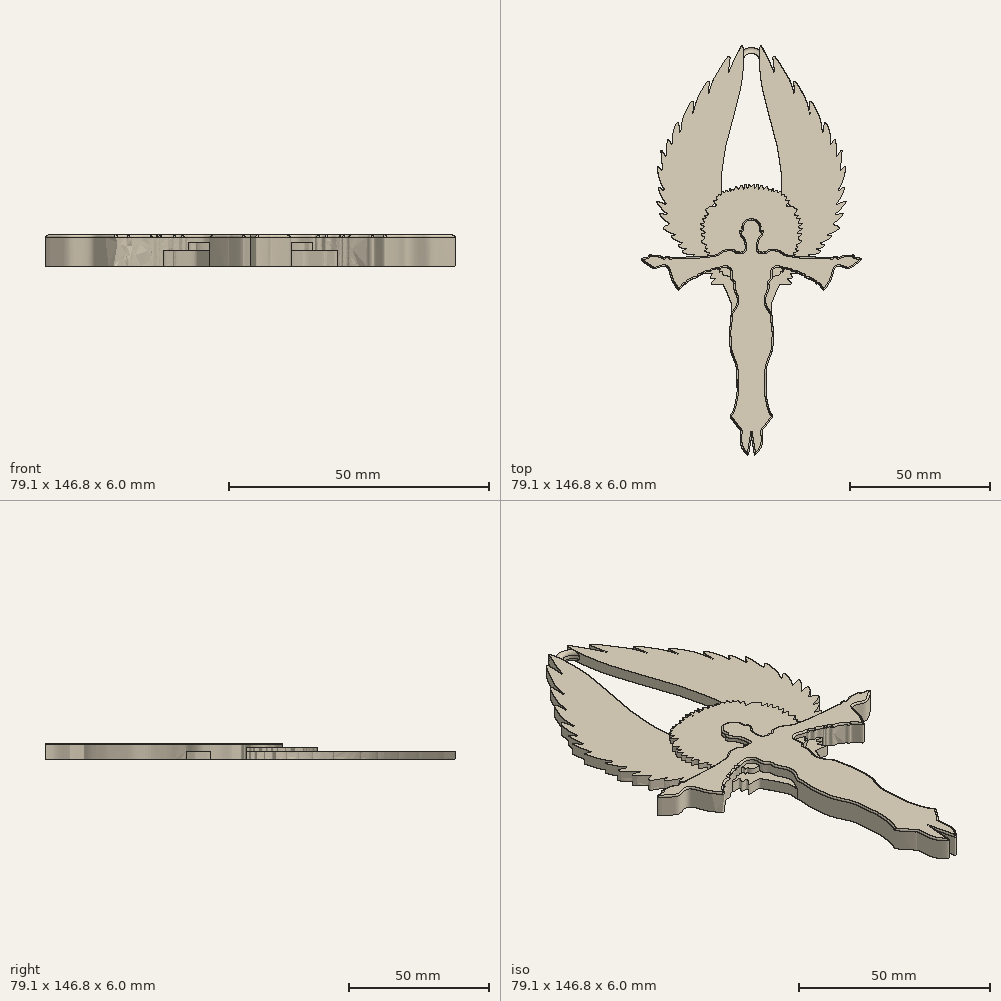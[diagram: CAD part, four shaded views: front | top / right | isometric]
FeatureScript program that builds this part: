
annotation { "Feature Type Name" : "Feature", "Feature Type Description" : "" }
export const myFeature = defineFeature(function(context is Context, id is Id, definition is map)
    precondition{}
    {
        {
            var Q0;
            Q0=qCreatedBy(makeId("Top.planeOp"),FACE);
            var sketch = newSketch(context, id + "F0", { "sketchPlane" : qUnion([Q0])});
            skFitSpline(sketch, "E0", {"points": [v(-21.33, -2.16) * mm, v(-20.52, -1.35) * mm, v(-22.98, -1.12) * mm, v(-24.75, 0) * mm, v(-23.25, 0.65) * mm, v(-25.06, 1.11) * mm, v(-26.3, 1.92) * mm, v(-25.33, 2.5) * mm, v(-24.29, 2.65) * mm, v(-26.4, 3.58) * mm, v(-28.83, 5.35) * mm, v(-27.72, 5.54) * mm, v(-27.02, 5.62) * mm, v(-29.3, 6.7) * mm, v(-31.45, 8.2) * mm, v(-30.37, 9.12) * mm, v(-29.37, 9.58) * mm, v(-30.99, 10.97) * mm, v(-32.37, 12.4) * mm, v(-32.76, 13.35) * mm, v(-31.49, 13.31) * mm, v(-30.02, 12.97) * mm, v(-30.99, 14) * mm, v(-32.41, 15.47) * mm, v(-33.64, 17.12) * mm, v(-33.8, 17.74) * mm, v(-32.81, 17.59) * mm, v(-31.91, 17.22) * mm, v(-30.93, 16.86) * mm, v(-30.6, 16.84) * mm, v(-31.6, 18.41) * mm, v(-33.2, 21.9) * mm, v(-33.18, 22.76) * mm, v(-31.72, 21.92) * mm, v(-31.03, 21.42) * mm, v(-31.56, 22.72) * mm, v(-32.62, 24.76) * mm, v(-33.08, 26.25) * mm, v(-33.57, 28.3) * mm, v(-33.66, 30.2) * mm, v(-32.2, 29.2) * mm, v(-31.8, 28.92) * mm, v(-32, 31) * mm, v(-32.33, 33.39) * mm, v(-32.4, 35.12) * mm, v(-32.31, 36.12) * mm, v(-30.9, 34.3) * mm, v(-30.43, 33.64) * mm, v(-30.4, 36.68) * mm, v(-29.8, 39.87) * mm, v(-28.95, 38.66) * mm, v(-28.45, 38) * mm, v(-28.22, 41.41) * mm, v(-26.52, 45.95) * mm, v(-25.73, 43.9) * mm, v(-25.46, 41.1) * mm, v(-25.1, 44.9) * mm, v(-24.15, 48.57) * mm, v(-22.3, 52.28) * mm, v(-21.1, 53.69) * mm, v(-20.86, 50.69) * mm, v(-21, 48.88) * mm, v(-19.92, 52.94) * mm, v(-18.25, 56.71) * mm, v(-16.96, 58.96) * mm, v(-15.69, 60.71) * mm, v(-15.17, 60.77) * mm, v(-15.48, 57.42) * mm, v(-15.46, 55.7) * mm, v(-14.9, 57.77) * mm, v(-13.72, 61.06) * mm, v(-12.05, 64.06) * mm, v(-10.2, 67.06) * mm, v(-7.78, 69.76) * mm, v(-8.32, 63.72) * mm, v(-7.03, 66.54) * mm, v(-5.58, 69.45) * mm, v(-4.06, 72.41) * mm, v(-3.33, 73.63) * mm, v(-2.81, 69.28) * mm, v(-3.1, 63.58) * mm, v(-3.86, 58.23) * mm, v(-6.75, 47.11) * mm, v(-8.79, 39.45) * mm, v(-9.63, 35.1) * mm, v(-10.4, 30.06) * mm, v(-10.79, 24.29) * mm, v(-11.22, 18.83) * mm, v(-13.02, 17.07) * mm, v(-15.43, 13.5) * mm, v(-16.47, 8.9) * mm, v(-16.23, 3.26) * mm, v(-14.7, 0) * mm, v(-13.5, -1.24) * mm, v(-17.7, -1.98) * mm, v(-21.33, -2.16) * mm]});
            skFitSpline(sketch, "E1.MirrorC", {"points": [v(21.33, -2.16) * mm, v(20.52, -1.35) * mm, v(22.98, -1.12) * mm, v(24.75, 0) * mm, v(23.25, 0.65) * mm, v(25.06, 1.11) * mm, v(26.3, 1.92) * mm, v(25.33, 2.5) * mm, v(24.29, 2.65) * mm, v(26.4, 3.58) * mm, v(28.83, 5.35) * mm, v(27.72, 5.54) * mm, v(27.02, 5.62) * mm, v(29.3, 6.7) * mm, v(31.45, 8.2) * mm, v(30.37, 9.12) * mm, v(29.37, 9.58) * mm, v(30.99, 10.97) * mm, v(32.37, 12.4) * mm, v(32.76, 13.35) * mm, v(31.49, 13.31) * mm, v(30.02, 12.97) * mm, v(30.99, 14) * mm, v(32.41, 15.47) * mm, v(33.64, 17.12) * mm, v(33.8, 17.74) * mm, v(32.81, 17.59) * mm, v(31.91, 17.22) * mm, v(30.93, 16.86) * mm, v(30.6, 16.84) * mm, v(31.6, 18.41) * mm, v(33.2, 21.9) * mm, v(33.18, 22.76) * mm, v(31.72, 21.92) * mm, v(31.03, 21.42) * mm, v(31.56, 22.72) * mm, v(32.62, 24.76) * mm, v(33.08, 26.25) * mm, v(33.57, 28.3) * mm, v(33.66, 30.2) * mm, v(32.2, 29.2) * mm, v(31.8, 28.92) * mm, v(32, 31) * mm, v(32.33, 33.39) * mm, v(32.4, 35.12) * mm, v(32.31, 36.12) * mm, v(30.9, 34.3) * mm, v(30.43, 33.64) * mm, v(30.4, 36.68) * mm, v(29.8, 39.87) * mm, v(28.95, 38.66) * mm, v(28.45, 38) * mm, v(28.22, 41.41) * mm, v(26.52, 45.95) * mm, v(25.73, 43.9) * mm, v(25.46, 41.1) * mm, v(25.1, 44.9) * mm, v(24.15, 48.57) * mm, v(22.3, 52.28) * mm, v(21.1, 53.69) * mm, v(20.86, 50.69) * mm, v(21, 48.88) * mm, v(19.92, 52.94) * mm, v(18.25, 56.71) * mm, v(16.96, 58.96) * mm, v(15.69, 60.71) * mm, v(15.17, 60.77) * mm, v(15.48, 57.42) * mm, v(15.46, 55.7) * mm, v(14.9, 57.77) * mm, v(13.72, 61.06) * mm, v(12.05, 64.06) * mm, v(10.2, 67.06) * mm, v(7.78, 69.76) * mm, v(8.32, 63.72) * mm, v(7.03, 66.54) * mm, v(5.58, 69.45) * mm, v(4.06, 72.41) * mm, v(3.33, 73.63) * mm, v(2.81, 69.28) * mm, v(3.1, 63.58) * mm, v(3.86, 58.23) * mm, v(6.75, 47.11) * mm, v(8.79, 39.45) * mm, v(9.63, 35.1) * mm, v(10.4, 30.06) * mm, v(10.79, 24.29) * mm, v(11.22, 18.83) * mm, v(13.02, 17.07) * mm, v(15.43, 13.5) * mm, v(16.47, 8.9) * mm, v(16.23, 3.26) * mm, v(14.7, 0) * mm, v(13.5, -1.24) * mm, v(17.7, -1.98) * mm, v(21.33, -2.16) * mm]});
            skFitSpline(sketch, "E2", {"points": [v(-7.41, -6.94) * mm, v(-8.3, -6.02) * mm, v(-9.37, -5.64) * mm, v(-12.12, -6.29) * mm, v(-12.64, -6.26) * mm, v(-13, -6.64) * mm, v(-13.92, -6.53) * mm, v(-14.54, -7.27) * mm, v(-15.6, -7.27) * mm, v(-16.72, -7.9) * mm, v(-16.15, -8.17) * mm, v(-14.08, -8.08) * mm, v(-14.76, -9.36) * mm, v(-14.54, -9.74) * mm, v(-13.02, -9.7) * mm, v(-14.06, -11.3) * mm, v(-14.42, -12.05) * mm, v(-10.7, -11.82) * mm, v(-9.9, -12.71) * mm, v(-8.87, -14.73) * mm, v(-7.46, -18.08) * mm, v(-6.98, -20) * mm, v(-7.21, -22.62) * mm, v(-5.94, -20.42) * mm, v(-5.19, -18.88) * mm, v(-4.95, -17.2) * mm, v(-5.74, -14.9) * mm, v(-6.24, -13.12) * mm, v(-6.22, -11.32) * mm, v(-7.01, -10.4) * mm, v(-7.4, -9.53) * mm, v(-7.41, -6.94) * mm]});
            skFitSpline(sketch, "E3.MirrorC", {"points": [v(7.41, -6.94) * mm, v(8.3, -6.02) * mm, v(9.37, -5.64) * mm, v(12.12, -6.29) * mm, v(12.64, -6.26) * mm, v(13, -6.64) * mm, v(13.92, -6.53) * mm, v(14.54, -7.27) * mm, v(15.6, -7.27) * mm, v(16.72, -7.9) * mm, v(16.15, -8.17) * mm, v(14.08, -8.08) * mm, v(14.76, -9.36) * mm, v(14.54, -9.74) * mm, v(13.02, -9.7) * mm, v(14.06, -11.3) * mm, v(14.42, -12.05) * mm, v(10.7, -11.82) * mm, v(9.9, -12.71) * mm, v(8.87, -14.73) * mm, v(7.46, -18.08) * mm, v(6.98, -20) * mm, v(7.21, -22.62) * mm, v(5.94, -20.42) * mm, v(5.19, -18.88) * mm, v(4.95, -17.2) * mm, v(5.74, -14.9) * mm, v(6.24, -13.12) * mm, v(6.22, -11.32) * mm, v(7.01, -10.4) * mm, v(7.4, -9.53) * mm, v(7.41, -6.94) * mm]});
            skSolve(sketch);
        }
        {
            var Q0;
            Q0=qCreatedBy(makeId("Top.planeOp"),FACE);
            var sketch = newSketch(context, id + "F1", { "sketchPlane" : qUnion([Q0])});
            skFitSpline(sketch, "E4", {"points": [v(0, -66.57) * mm, v(-0.96, -72.4) * mm, v(-1.25, -73.17) * mm, v(-2.87, -71.43) * mm, v(-3.9, -68.45) * mm, v(-3.9, -64.18) * mm, v(-4.13, -63.88) * mm, v(-6.43, -61.04) * mm, v(-7.6, -59.39) * mm, v(-7.63, -59.2) * mm, v(-6.72, -57.5) * mm, v(-5.78, -54.37) * mm, v(-5.23, -51.26) * mm, v(-5.17, -47.57) * mm, v(-5.2, -44.7) * mm, v(-5.33, -42.23) * mm, v(-6.07, -39.55) * mm, v(-7.47, -35.63) * mm, v(-7.82, -31.71) * mm, v(-7.8, -27.67) * mm, v(-7.34, -24.2) * mm, v(-7.24, -22.62) * mm, v(-5.91, -20.4) * mm, v(-5.2, -18.84) * mm, v(-5.02, -17.26) * mm, v(-5.8, -14.88) * mm, v(-6.35, -13.1) * mm, v(-6.3, -11.38) * mm, v(-7.06, -10.47) * mm, v(-7.47, -9.55) * mm, v(-7.5, -7) * mm, v(-8.34, -6.1) * mm, v(-9.35, -5.73) * mm, v(-12.1, -6.41) * mm, v(-12.53, -6.32) * mm, v(-12.99, -6.73) * mm, v(-13.8, -6.57) * mm, v(-14.54, -7.4) * mm, v(-15.5, -7.3) * mm, v(-16.67, -7.9) * mm, v(-17.1, -8.02) * mm, v(-17.24, -8.18) * mm, v(-17.68, -8.22) * mm, v(-17.86, -8.52) * mm, v(-18.48, -8.57) * mm, v(-18.91, -8.82) * mm, v(-19, -9.37) * mm, v(-20.58, -9.76) * mm, v(-20.93, -9.82) * mm, v(-22.3, -10.65) * mm, v(-22.76, -11.01) * mm, v(-22.94, -11.45) * mm, v(-23.58, -11.8) * mm, v(-23.97, -11.75) * mm, v(-25.85, -14.13) * mm, v(-26.46, -13.67) * mm, v(-28.64, -9.96) * mm, v(-30.3, -5.68) * mm, v(-32.58, -5.68) * mm, v(-34.7, -6.3) * mm, v(-36.63, -5.38) * mm, v(-39.07, -3.5) * mm, v(-39.5, -2.78) * mm, v(-37.88, -2.34) * mm, v(-36.8, -2.02) * mm, v(-36.79, -1.5) * mm, v(-35.69, -1.4) * mm, v(-33.35, -1.5) * mm, v(-31.57, -2.3) * mm, v(-30.93, -2.32) * mm, v(-30.86, -1.95) * mm, v(-29.5, -1.93) * mm, v(-29.28, -2.36) * mm, v(-28.5, -2.32) * mm, v(-24.9, -2.2) * mm, v(-22.05, -2.18) * mm, v(-21, -2.16) * mm, v(-15.87, -1.84) * mm, v(-14.18, -1.52) * mm, v(-12.66, -1.31) * mm, v(-10.95, -0.42) * mm, v(-9.48, 0.38) * mm, v(-6.7, 0.57) * mm, v(-5.62, 0) * mm, v(-5.27, -0.46) * mm, v(-4.95, -0.19) * mm, v(-4.65, 0) * mm, v(-4.13, -0.46) * mm, v(-3.56, -0.17) * mm, v(-3.14, 0) * mm, v(-2.8, -0.26) * mm, v(-2.37, 0.38) * mm, v(-2.34, 2.56) * mm, v(-3.08, 4.52) * mm, v(-3.85, 5.42) * mm, v(-4.2, 6.88) * mm, v(-4.01, 7.45) * mm, v(-3.46, 7.34) * mm, v(-3.4, 8.74) * mm, v(-2.62, 10.27) * mm, v(-1.36, 11.32) * mm, v(0, 11.6) * mm], "startDerivative": vector(-60, -350.77) * mm, "endDerivative": vector(147.12, 11.85) * mm});
            skFitSpline(sketch, "E5.MirrorCS", {"points": [v(0, -66.57) * mm, v(0.96, -72.4) * mm, v(1.25, -73.17) * mm, v(2.87, -71.43) * mm, v(3.9, -68.45) * mm, v(3.9, -64.18) * mm, v(4.13, -63.88) * mm, v(6.43, -61.04) * mm, v(7.6, -59.39) * mm, v(7.63, -59.2) * mm, v(6.72, -57.5) * mm, v(5.78, -54.37) * mm, v(5.23, -51.26) * mm, v(5.17, -47.57) * mm, v(5.2, -44.7) * mm, v(5.33, -42.23) * mm, v(6.07, -39.55) * mm, v(7.47, -35.63) * mm, v(7.82, -31.71) * mm, v(7.8, -27.67) * mm, v(7.34, -24.2) * mm, v(7.24, -22.62) * mm, v(5.91, -20.4) * mm, v(5.2, -18.84) * mm, v(5.02, -17.26) * mm, v(5.8, -14.88) * mm, v(6.35, -13.1) * mm, v(6.3, -11.38) * mm, v(7.06, -10.47) * mm, v(7.47, -9.55) * mm, v(7.5, -7) * mm, v(8.34, -6.1) * mm, v(9.35, -5.73) * mm, v(12.1, -6.41) * mm, v(12.53, -6.32) * mm, v(12.99, -6.73) * mm, v(13.8, -6.57) * mm, v(14.54, -7.4) * mm, v(15.5, -7.3) * mm, v(16.67, -7.9) * mm, v(17.1, -8.02) * mm, v(17.24, -8.18) * mm, v(17.68, -8.22) * mm, v(17.86, -8.52) * mm, v(18.48, -8.57) * mm, v(18.91, -8.82) * mm, v(19, -9.37) * mm, v(20.58, -9.76) * mm, v(20.93, -9.82) * mm, v(22.3, -10.65) * mm, v(22.76, -11.01) * mm, v(22.94, -11.45) * mm, v(23.58, -11.8) * mm, v(23.97, -11.75) * mm, v(25.85, -14.13) * mm, v(26.46, -13.67) * mm, v(28.64, -9.96) * mm, v(30.3, -5.68) * mm, v(32.58, -5.68) * mm, v(34.7, -6.3) * mm, v(36.63, -5.38) * mm, v(39.07, -3.5) * mm, v(39.5, -2.78) * mm, v(37.88, -2.34) * mm, v(36.8, -2.02) * mm, v(36.79, -1.5) * mm, v(35.69, -1.4) * mm, v(33.35, -1.5) * mm, v(31.57, -2.3) * mm, v(30.93, -2.32) * mm, v(30.86, -1.95) * mm, v(29.5, -1.93) * mm, v(29.28, -2.36) * mm, v(28.5, -2.32) * mm, v(24.9, -2.2) * mm, v(22.05, -2.18) * mm, v(21, -2.16) * mm, v(15.87, -1.84) * mm, v(14.18, -1.52) * mm, v(12.66, -1.31) * mm, v(10.95, -0.42) * mm, v(9.48, 0.38) * mm, v(6.7, 0.57) * mm, v(5.62, 0) * mm, v(5.27, -0.46) * mm, v(4.95, -0.19) * mm, v(4.65, 0) * mm, v(4.13, -0.46) * mm, v(3.56, -0.17) * mm, v(3.14, 0) * mm, v(2.8, -0.26) * mm, v(2.37, 0.38) * mm, v(2.34, 2.56) * mm, v(3.08, 4.52) * mm, v(3.85, 5.42) * mm, v(4.2, 6.88) * mm, v(4.01, 7.45) * mm, v(3.46, 7.34) * mm, v(3.4, 8.74) * mm, v(2.62, 10.27) * mm, v(1.36, 11.32) * mm, v(0, 11.6) * mm], "startDerivative": vector(60, -350.77) * mm, "endDerivative": vector(-147.12, 11.85) * mm});
            skSolve(sketch);
        }
        {
            var Q0;
            Q0=qCreatedBy(makeId("Top.planeOp"),FACE);
            var sketch = newSketch(context, id + "F2", { "sketchPlane" : qUnion([Q0])});
            skFitSpline(sketch, "E6", {"points": [v(0, -7.8) * mm, v(-8.65, -8.9) * mm, v(-10.45, -8) * mm, v(-10.45, -7.25) * mm, v(-11.45, -7.6) * mm, v(-11.1, -6.6) * mm, v(-11.95, -6.4) * mm, v(-14.96, -1.7) * mm, v(-15.91, -1.44) * mm, v(-14.8, -0.84) * mm, v(-16.81, 0) * mm, v(-15.76, 0.76) * mm, v(-16.66, 1.31) * mm, v(-15.96, 1.96) * mm, v(-17.96, 3.32) * mm, v(-16.66, 4.57) * mm, v(-18.06, 6.07) * mm, v(-16.36, 6.47) * mm, v(-18.16, 7.87) * mm, v(-16.91, 8.47) * mm, v(-18.11, 9.78) * mm, v(-16.76, 10.18) * mm, v(-17.71, 11.78) * mm, v(-16.01, 11.58) * mm, v(-17.01, 12.88) * mm, v(-15.46, 12.88) * mm, v(-16.31, 14.68) * mm, v(-15.6, 15.28) * mm, v(-14.26, 16.09) * mm, v(-12.56, 16.34) * mm, v(-13.7, 18.19) * mm, v(-12.25, 18.04) * mm, v(-12.76, 19.24) * mm, v(-11.95, 19.54) * mm, v(-11.8, 20.5) * mm, v(-10.85, 20) * mm, v(-10.6, 21.4) * mm, v(-9.45, 20.94) * mm, v(-9.1, 21.8) * mm, v(-8.1, 21.34) * mm, v(-7.75, 22.4) * mm, v(-7.3, 21.5) * mm, v(-6.75, 22.24) * mm, v(-6.25, 21.64) * mm, v(-5.54, 23.05) * mm, v(-4.54, 22.1) * mm, v(-3.64, 23.6) * mm, v(-2.7, 22.14) * mm, v(-2.19, 24.1) * mm, v(-1.34, 22.1) * mm, v(-0.99, 23.7) * mm, v(0, 22.95) * mm], "startDerivative": vector(-212.24, -41.93) * mm, "endDerivative": vector(67.77, -87.85) * mm});
            skFitSpline(sketch, "E7.MirrorCS", {"points": [v(0, -7.8) * mm, v(8.65, -8.9) * mm, v(10.45, -8) * mm, v(10.45, -7.25) * mm, v(11.45, -7.6) * mm, v(11.1, -6.6) * mm, v(11.95, -6.4) * mm, v(14.96, -1.7) * mm, v(15.91, -1.44) * mm, v(14.8, -0.84) * mm, v(16.81, 0) * mm, v(15.76, 0.76) * mm, v(16.66, 1.31) * mm, v(15.96, 1.96) * mm, v(17.96, 3.32) * mm, v(16.66, 4.57) * mm, v(18.06, 6.07) * mm, v(16.36, 6.47) * mm, v(18.16, 7.87) * mm, v(16.91, 8.47) * mm, v(18.11, 9.78) * mm, v(16.76, 10.18) * mm, v(17.71, 11.78) * mm, v(16.01, 11.58) * mm, v(17.01, 12.88) * mm, v(15.46, 12.88) * mm, v(16.31, 14.68) * mm, v(15.6, 15.28) * mm, v(14.26, 16.09) * mm, v(12.56, 16.34) * mm, v(13.7, 18.19) * mm, v(12.25, 18.04) * mm, v(12.76, 19.24) * mm, v(11.95, 19.54) * mm, v(11.8, 20.5) * mm, v(10.85, 20) * mm, v(10.6, 21.4) * mm, v(9.45, 20.94) * mm, v(9.1, 21.8) * mm, v(8.1, 21.34) * mm, v(7.75, 22.4) * mm, v(7.3, 21.5) * mm, v(6.75, 22.24) * mm, v(6.25, 21.64) * mm, v(5.54, 23.05) * mm, v(4.54, 22.1) * mm, v(3.64, 23.6) * mm, v(2.7, 22.14) * mm, v(2.19, 24.1) * mm, v(1.34, 22.1) * mm, v(0.99, 23.7) * mm, v(0, 22.95) * mm], "startDerivative": vector(212.24, -41.93) * mm, "endDerivative": vector(-67.77, -87.85) * mm});
            skSolve(sketch);
        }
        {
            var Q0;
            Q0=makeQuery(id+"F0.imprint","IMPRINT",FACE,{"disambiguationData":[TD([[makeQuery(id+"F0.imprint","IMPRINT",EDGE,{"derivedFrom":sQuery(id+"F0.wireOp",EDGE,"E0")}),-1.0]])]});
            var Q1;
            Q1=makeQuery(id+"F0.imprint","IMPRINT",FACE,{"disambiguationData":[TD([[makeQuery(id+"F0.imprint","IMPRINT",EDGE,{"derivedFrom":sQuery(id+"F0.wireOp",EDGE,"E1.MirrorC")}),1.0]])]});
            var Q2;
            Q2=makeQuery(id+"F0.imprint","IMPRINT",FACE,{"disambiguationData":[TD([[makeQuery(id+"F0.imprint","IMPRINT",EDGE,{"derivedFrom":sQuery(id+"F0.wireOp",EDGE,"E2")}),1.0]])]});
            var Q3;
            Q3=makeQuery(id+"F0.imprint","IMPRINT",FACE,{"disambiguationData":[TD([[makeQuery(id+"F0.imprint","IMPRINT",EDGE,{"derivedFrom":sQuery(id+"F0.wireOp",EDGE,"E3.MirrorC")}),-1.0]])]});
            extrude(context, id + "F3", {"entities" : qUnion([Q0, Q1, Q2, Q3]), "depth" : 3 * mm});
        }
        {
            var Q0;
            Q0=makeQuery(id+"F2.imprint","IMPRINT",FACE,{"disambiguationData":[TD([[makeQuery(id+"F2.imprint","IMPRINT",EDGE,{"derivedFrom":sQuery(id+"F2.wireOp",EDGE,"E6")}),-1.0]])]});
            extrude(context, id + "F4", {"entities" : qUnion([Q0]), "operationType" : NewBodyOperationType.ADD, "depth" : 4.5 * mm});
        }
        {
            var Q0;
            Q0=makeQuery(id+"F1.imprint","IMPRINT",FACE,{"disambiguationData":[TD([[makeQuery(id+"F1.imprint","IMPRINT",EDGE,{"derivedFrom":sQuery(id+"F1.wireOp",EDGE,"E4")}),-1.0]])]});
            extrude(context, id + "F5", {"entities" : qUnion([Q0]), "operationType" : NewBodyOperationType.ADD, "depth" : 6 * mm});
        }
        {
            var Q0;
            Q0=makeQuery(id+"F5.opExtrude","CAP_FACE",FACE,{"disambiguationData":[OSD([sQuery(id+"F1.wireOp",EDGE,"E4"),sQuery(id+"F1.wireOp",EDGE,"E5.MirrorCS")])],"isStart":false});
            fillet(context, id + "F6", {"entities" : qUnion([Q0]), "radius" : 0.5 * mm, "tangentPropagation" : true, "allowEdgeOverflow" : false});
        }
        {
            var Q0;
            Q0=qCreatedBy(makeId("Top.planeOp"),FACE);
            var sketch = newSketch(context, id + "F7", { "sketchPlane" : qUnion([Q0])});
            skArc(sketch, "E8", {"start": v(4.86, 68) * mm, "mid": v(0, 72.86) * mm, "end": v(-4.86, 68) * mm});
            skArc(sketch, "E9", {"start": v(2.86, 68) * mm, "mid": v(0, 70.86) * mm, "end": v(-2.86, 68) * mm});
            skLineSegment(sketch, "E10", {"start": v(-4.86, 68) * mm, "end": v(4.86, 68) * mm, "construction": true});
            skLineSegment(sketch, "E11", {"start": v(0, 0) * mm, "end": v(0, 68) * mm, "construction": true});
            skLineSegment(sketch, "E12", {"start": v(-4.86, 68) * mm, "end": v(-2.86, 68) * mm});
            skLineSegment(sketch, "E13", {"start": v(2.86, 68) * mm, "end": v(4.86, 68) * mm});
            skSolve(sketch);
        }
        {
            var Q0;
            Q0=makeQuery(id+"F7.imprint","IMPRINT",FACE,{"disambiguationData":[TD([[makeQuery(id+"F7.imprint","IMPRINT",EDGE,{"derivedFrom":sQuery(id+"F7.wireOp",EDGE,"E8")}),1.0]])]});
            extrude(context, id + "F8", {"entities" : qUnion([Q0]), "operationType" : NewBodyOperationType.ADD, "depth" : 3 * mm});
        }
        {
            var Q0;
            Q0=makeQuery(id+"F8.opExtrude","CAP_EDGE",EDGE,{"disambiguationData":[OSD([sQuery(id+"F7.wireOp",EDGE,"E8")])],"isStart":false});
            var Q1;
            Q1=makeQuery(id+"F8.opExtrude","CAP_EDGE",EDGE,{"disambiguationData":[OSD([sQuery(id+"F7.wireOp",EDGE,"E8")])],"isStart":true});
            var Q2;
            Q2=makeQuery(id+"F8.opExtrude","CAP_EDGE",EDGE,{"disambiguationData":[OSD([sQuery(id+"F7.wireOp",EDGE,"E9")])],"isStart":true});
            var Q3;
            Q3=makeQuery(id+"F8.opExtrude","CAP_EDGE",EDGE,{"disambiguationData":[OSD([sQuery(id+"F7.wireOp",EDGE,"E9")])],"isStart":false});
            fillet(context, id + "F9", {"entities" : qUnion([Q0, Q1, Q2, Q3]), "radius" : 1 * mm, "tangentPropagation" : true, "allowEdgeOverflow" : false});
        }
    });
